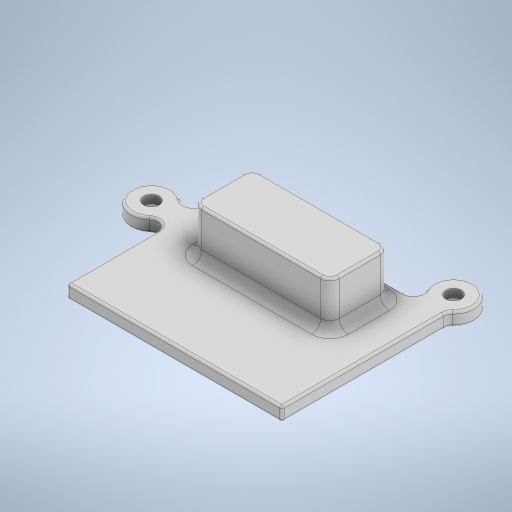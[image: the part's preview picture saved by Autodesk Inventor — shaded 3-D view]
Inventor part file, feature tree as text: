
AUTODESK INVENTOR PART (.ipt)
format: ipt  version: 2024.2 (Build 282272000, 272)  size: 409,088 bytes
history: native  units: mm
features: extrude x4, sketch x4, fillet x3
ambient origin geometry x8: Origin, YZ Plane, XZ Plane, XY Plane, X Axis, Y Axis, Z Axis, Center Point
bodies: Solid1 (feature_tree)
feature tree (11):
  extrude  "Extrusion1"  Depth=35.0mm
  extrude  "Extrusion3"  Depth=5.0mm
  extrude  "Extrusion4"  Depth=3.0mm TaperAngle=0.0deg
  fillet  "Fillet4"  Radius=2.5mm
  fillet  "Fillet5"  Radius=5.0mm
  fillet  "Fillet6"  Radius=50.8mm
  extrude  "Extrusion5"  Depth=2.5mm
  sketch  "Sketch1"  dims[d0=47.0mm d1=35.0mm]
  sketch  "Sketch3"  dims[d3=3.4mm d4=5.0mm]
  sketch  "Sketch4"  dims[d5=9.0mm d6=3.0mm d7=0.0mm d17=2.5mm d18=5.0mm d19=50.8mm]
  sketch  "Sketch5"  dims[d20=5.0mm d21=2.5mm d22=15.2mm d23=5.7mm d24=1.0mm d25=0.0mm d26=30.0mm d27=13.0mm d28=3.0mm d29=10.0mm d30=0.0mm d31=2.0mm d32=0.5mm d33=0.5mm d34=0.2mm d35=0.0mm]
